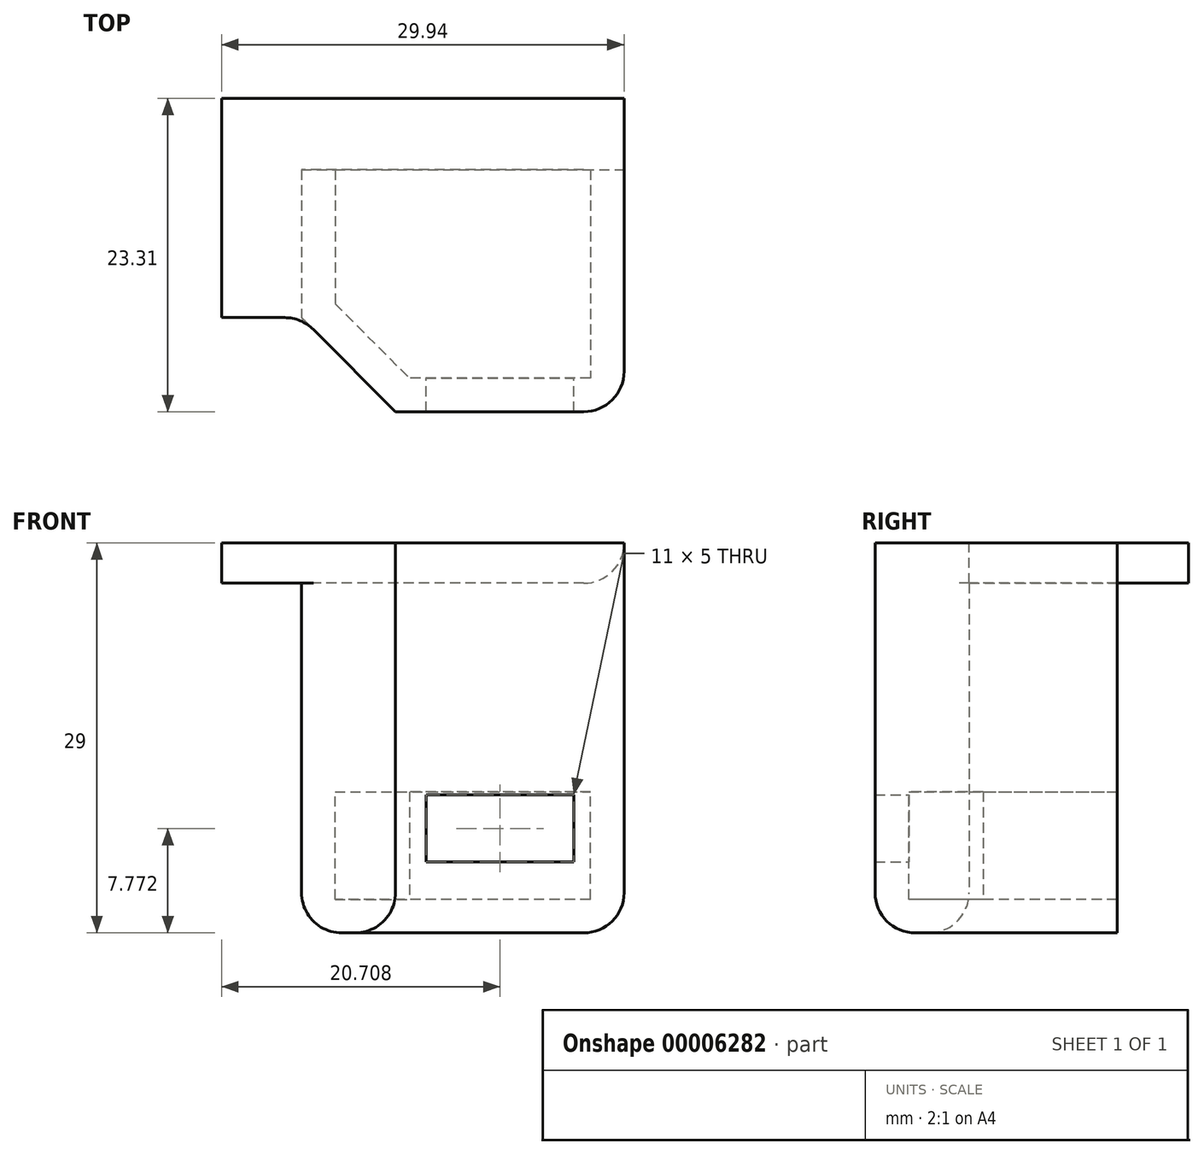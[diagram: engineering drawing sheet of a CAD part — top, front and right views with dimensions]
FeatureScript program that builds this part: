
annotation { "Feature Type Name" : "Feature", "Feature Type Description" : "" }
export const myFeature = defineFeature(function(context is Context, id is Id, definition is map)
    precondition{}
    {
        {
            var Q0;
            Q0=qCreatedBy(makeId("Front.planeOp"),FACE);
            var sketch = newSketch(context, id + "F0", { "sketchPlane" : qUnion([Q0])});
            skLineSegment(sketch, "E0.rect.bottom", {"start": v(12, -14.5) * mm, "end": v(-12, -14.5) * mm});
            skLineSegment(sketch, "E0.rect.top", {"start": v(12, 14.5) * mm, "end": v(-12, 14.5) * mm});
            skLineSegment(sketch, "E0.rect.left", {"start": v(12, -14.5) * mm, "end": v(12, 14.5) * mm});
            skLineSegment(sketch, "E0.rect.right", {"start": v(-12, -14.5) * mm, "end": v(-12, 14.5) * mm});
            skPoint(sketch, "E0.rect.middle", {"position": v(0, 0) * mm});
            skLineSegment(sketch, "E1.rect.bottom", {"start": v(9.3, 4.77) * mm, "end": v(-9.3, 4.77) * mm});
            skLineSegment(sketch, "E1.rect.top", {"start": v(9.3, 12.77) * mm, "end": v(-9.3, 12.77) * mm});
            skLineSegment(sketch, "E1.rect.left", {"start": v(9.3, 4.77) * mm, "end": v(9.3, 12.77) * mm});
            skLineSegment(sketch, "E1.rect.right", {"start": v(-9.3, 4.77) * mm, "end": v(-9.3, 12.77) * mm});
            skPoint(sketch, "E1.rect.middle", {"position": v(0, 8.77) * mm});
            skSolve(sketch);
        }
        {
            var Q0;
            Q0=makeQuery(id+"F0.imprint","IMPRINT",FACE,{"disambiguationData":[TD([[makeQuery(id+"F0.imprint","IMPRINT",EDGE,{"derivedFrom":sQuery(id+"F0.wireOp",EDGE,"E0.rect.bottom")}),-1.0]])]});
            var Q1;
            Q1=makeQuery(id+"F0.imprint","IMPRINT",FACE,{"disambiguationData":[TD([[makeQuery(id+"F0.imprint","IMPRINT",EDGE,{"derivedFrom":sQuery(id+"F0.wireOp",EDGE,"E1.rect.bottom")}),-1.0]])]});
            extrude(context, id + "F1", {"entities" : qUnion([Q0, Q1]), "depth" : 18 * mm});
        }
        {
            var Q0;
            Q0=makeQuery(id+"F1.opExtrude","SWEPT_FACE",FACE,{"disambiguationData":[OSD([sQuery(id+"F0.wireOp",EDGE,"E0.rect.bottom")])]});
            var sketch = newSketch(context, id + "F2", { "sketchPlane" : qUnion([Q0])});
            skLineSegment(sketch, "E2", {"start": v(-12, 7) * mm, "end": v(-5, 0) * mm});
            skLineSegment(sketch, "E3", {"start": v(-5, 0) * mm, "end": v(-12, 0) * mm});
            skLineSegment(sketch, "E4", {"start": v(-12, 0) * mm, "end": v(-12, 7) * mm});
            skSolve(sketch);
        }
        {
            var Q0;
            Q0=makeQuery(id+"F2.imprint","IMPRINT",FACE,{"disambiguationData":[TD([[makeQuery(id+"F2.imprint","IMPRINT",EDGE,{"derivedFrom":sQuery(id+"F2.wireOp",EDGE,"E2")}),-1.0]])]});
            extrude(context, id + "F3", {"entities" : qUnion([Q0]), "operationType" : NewBodyOperationType.REMOVE, "endBound" : BoundingType.THROUGH_ALL, "oppositeDirection" : true, "depth" : 25 * mm});
        }
        {
            var Q0;
            Q0=makeQuery(id+"F1.opExtrude","CAP_FACE",FACE,{"disambiguationData":[OSD([sQuery(id+"F0.wireOp",EDGE,"E0.rect.bottom"),sQuery(id+"F0.wireOp",EDGE,"E0.rect.top"),sQuery(id+"F0.wireOp",EDGE,"E0.rect.left"),sQuery(id+"F0.wireOp",EDGE,"E0.rect.right")])],"isStart":false});
            shell(context, id + "F4", {"entities" : qUnion([Q0]), "thickness" : 2.5 * mm});
        }
        {
            var Q0;
            Q0=makeQuery(id+"F1.opExtrude","CAP_FACE",FACE,{"disambiguationData":[OSD([sQuery(id+"F0.wireOp",EDGE,"E0.rect.bottom"),sQuery(id+"F0.wireOp",EDGE,"E0.rect.top"),sQuery(id+"F0.wireOp",EDGE,"E0.rect.left"),sQuery(id+"F0.wireOp",EDGE,"E0.rect.right")])],"isStart":false});
            var sketch = newSketch(context, id + "F5", { "sketchPlane" : qUnion([Q0])});
            skLineSegment(sketch, "E5.top", {"start": v(-9.5, -4) * mm, "end": v(9.5, -4) * mm});
            skLineSegment(sketch, "E6.0", {"start": v(12, -14.5) * mm, "end": v(12, 14.5) * mm});
            skLineSegment(sketch, "E7", {"start": v(-9.5, -4) * mm, "end": v(-9.5, 12) * mm});
            skLineSegment(sketch, "E8", {"start": v(-9.5, 12) * mm, "end": v(9.5, 12) * mm});
            skLineSegment(sketch, "E9", {"start": v(9.5, 12) * mm, "end": v(9.5, -4) * mm});
            skSolve(sketch);
        }
        {
            var Q0;
            Q0=makeQuery(id+"F5.imprint","IMPRINT",FACE,{"disambiguationData":[TD([[makeQuery(id+"F5.imprint","IMPRINT",EDGE,{"derivedFrom":sQuery(id+"F5.wireOp",EDGE,"E5.top")}),1.0]])]});
            var Q1;
            Q1=makeQuery(id+"F1.opExtrude","SWEPT_BODY",BODY,{"disambiguationData":[OSD([sQuery(id+"F0.wireOp",EDGE,"E0.rect.bottom"),sQuery(id+"F0.wireOp",EDGE,"E0.rect.top"),sQuery(id+"F0.wireOp",EDGE,"E0.rect.left"),sQuery(id+"F0.wireOp",EDGE,"E0.rect.right")])]});
            extrude(context, id + "F6", {"entities" : qUnion([Q0]), "operationType" : NewBodyOperationType.ADD, "endBound" : BoundingType.UP_TO_BODY, "oppositeDirection" : true, "endBoundEntityBody" : qUnion([Q1]), "depth" : 25 * mm});
        }
        {
            var Q0;
            Q0=makeQuery(id+"F1.opExtrude","SWEPT_FACE",FACE,{"disambiguationData":[OSD([sQuery(id+"F0.wireOp",EDGE,"E0.rect.top")])]});
            var sketch = newSketch(context, id + "F7", { "sketchPlane" : qUnion([Q0])});
            skLineSegment(sketch, "E10.left", {"start": v(12, -18) * mm, "end": v(12, 0) * mm});
            skLineSegment(sketch, "E11.bottom", {"start": v(12, -18) * mm, "end": v(-12, -18) * mm});
            skLineSegment(sketch, "E11.top", {"start": v(12, -23.31) * mm, "end": v(-12, -23.31) * mm});
            skLineSegment(sketch, "E11.right", {"start": v(-12, -18) * mm, "end": v(-12, -23.31) * mm});
            skLineSegment(sketch, "E12.bottom", {"start": v(-12, -7) * mm, "end": v(-17.94, -7) * mm});
            skLineSegment(sketch, "E12.top", {"start": v(-12, -23.31) * mm, "end": v(-17.94, -23.31) * mm});
            skLineSegment(sketch, "E12.left", {"start": v(-12, -7) * mm, "end": v(-12, -23.31) * mm});
            skLineSegment(sketch, "E12.right", {"start": v(-17.94, -7) * mm, "end": v(-17.94, -23.31) * mm});
            skLineSegment(sketch, "E13", {"start": v(12, -18) * mm, "end": v(12, -23.31) * mm});
            skPoint(sketch, "E14.orphan", {"position": v(19.4, -23.31) * mm});
            skSolve(sketch);
        }
        {
            var Q0;
            Q0=makeQuery(id+"F7.imprint","IMPRINT",FACE,{"disambiguationData":[TD([[makeQuery(id+"F7.imprint","IMPRINT",EDGE,{"derivedFrom":sQuery(id+"F7.wireOp",EDGE,"E10.top")}),-1.0]])]});
            var Q1;
            {var subQ2=sQuery(id+"F7.wireOp",EDGE,"E11.bottom");Q1=makeQuery(id+"F7.imprint","IMPRINT",FACE,{"disambiguationData":[TD([[makeQuery(id+"F7.imprint","IMPRINT",EDGE,{"derivedFrom":subQ2}),1.0]])]});}
            var Q2;
            {var subQ3=sQuery(id+"F7.wireOp",EDGE,"E12.bottom");Q2=makeQuery(id+"F7.imprint","IMPRINT",FACE,{"disambiguationData":[TD([[makeQuery(id+"F7.imprint","IMPRINT",EDGE,{"derivedFrom":subQ3}),1.0]])]});}
            var Q3;
            Q3=makeQuery(id+"F7.imprint","IMPRINT",FACE,{"disambiguationData":[TD([[makeQuery(id+"F7.imprint","IMPRINT",EDGE,{"derivedFrom":sQuery(id+"F7.wireOp",EDGE,"E10.left")}),1.0]])]});
            extrude(context, id + "F8", {"entities" : qUnion([Q0, Q1, Q2, Q3]), "operationType" : NewBodyOperationType.ADD, "oppositeDirection" : true, "depth" : 3 * mm});
        }
        {
            var Q0;
            Q0=makeQuery(id+"F8.opExtrude","CAP_EDGE",EDGE,{"disambiguationData":[OSD([sQuery(id+"F7.wireOp",EDGE,"E10.left"),sQuery(id+"F7.wireOp",EDGE,"E13")])],"isStart":false});
            var Q1;
            Q1=makeQuery(id+"F8.opExtrude","CAP_EDGE",EDGE,{"disambiguationData":[OSD([sQuery(id+"F7.wireOp",EDGE,"E11.bottom")])],"isStart":false});
            fillet(context, id + "F9", {"entities" : qUnion([Q0, Q1]), "radius" : 3 * mm, "tangentPropagation" : true, "allowEdgeOverflow" : false});
        }
        {
            var Q0;
            Q0=makeQuery(id+"F1.opExtrude","CAP_EDGE",EDGE,{"disambiguationData":[OSD([sQuery(id+"F0.wireOp",EDGE,"E0.rect.bottom")])],"isStart":true});
            var Q1;
            Q1=makeQuery(id+"F1.opExtrude","SWEPT_EDGE",EDGE,{"disambiguationData":[OSD([sQuery(id+"F0.wireOp",EDGE,"E0.rect.bottom"),sQuery(id+"F0.wireOp",EDGE,"E0.rect.left")])]});
            var Q2;
            Q2=makeQuery(id+"F3.boolean.opBoolean","COPY",EDGE,{"derivedFrom":makeQuery(id+"F3.opExtrude","CAP_EDGE",EDGE,{"disambiguationData":[OSD([sQuery(id+"F2.wireOp",EDGE,"E2")])],"isStart":true})});
            var Q3;
            Q3=makeQuery(id+"F1.opExtrude","SWEPT_EDGE",EDGE,{"disambiguationData":[OSD([sQuery(id+"F0.wireOp",EDGE,"E0.rect.bottom"),sQuery(id+"F0.wireOp",EDGE,"E0.rect.right")])]});
            var Q4;
            Q4=makeQuery(id+"F1.opExtrude","CAP_EDGE",EDGE,{"disambiguationData":[OSD([sQuery(id+"F0.wireOp",EDGE,"E0.rect.left")])],"isStart":true});
            var Q5;
            Q5=makeQuery(id+"F3.boolean.opBoolean","COPY",EDGE,{"derivedFrom":makeQuery(id+"F3.opExtrude","SWEPT_EDGE",EDGE,{"disambiguationData":[OSD([sQuery(id+"F0.wireOp",EDGE,"E0.rect.bottom"),sQuery(id+"F2.wireOp",EDGE,"E2"),sQuery(id+"F2.wireOp",EDGE,"E3")])]})});
            var Q6;
            {var subQ0=sQuery(id+"F2.wireOp",EDGE,"E2");Q6=makeQuery(id+"F8.boolean.opBoolean","MERGE",EDGE,{"derivedFrom":[makeQuery(id+"F3.boolean.opBoolean","COPY",EDGE,{"derivedFrom":makeQuery(id+"F3.opExtrude","SWEPT_EDGE",EDGE,{"disambiguationData":[OSD([sQuery(id+"F0.wireOp",EDGE,"E0.rect.bottom"),sQuery(id+"F0.wireOp",EDGE,"E0.rect.right"),subQ0,sQuery(id+"F2.wireOp",EDGE,"E4")])]})}),makeQuery(id+"F8.opExtrude","SWEPT_EDGE",EDGE,{"disambiguationData":[OSD([sQuery(id+"F0.wireOp",EDGE,"E0.rect.top"),subQ0,sQuery(id+"F7.wireOp",EDGE,"E12.bottom"),sQuery(id+"F7.wireOp",EDGE,"E12.left")])]})]});}
            fillet(context, id + "F10", {"entities" : qUnion([Q0, Q1, Q2, Q3, Q4, Q5, Q6]), "radius" : 3 * mm, "tangentPropagation" : true, "allowEdgeOverflow" : false});
        }
        {
            var Q0;
            Q0=makeQuery(id+"F4.opShell","OFFSET_FACE",FACE,{"disambiguationData":[OSD([sQuery(id+"F0.wireOp",EDGE,"E0.rect.bottom"),sQuery(id+"F0.wireOp",EDGE,"E0.rect.top"),sQuery(id+"F0.wireOp",EDGE,"E0.rect.left"),sQuery(id+"F0.wireOp",EDGE,"E0.rect.right")])]});
            var sketch = newSketch(context, id + "F11", { "sketchPlane" : qUnion([Q0])});
            skLineSegment(sketch, "E15.0", {"start": v(9.5, -12) * mm, "end": v(-9.5, -12) * mm});
            skLineSegment(sketch, "E16.0", {"start": v(9.5, -12) * mm, "end": v(9.5, -4) * mm});
            skLineSegment(sketch, "E17.0", {"start": v(-9.5, -4) * mm, "end": v(9.5, -4) * mm});
            skLineSegment(sketch, "E18.0", {"start": v(-3.96, -4) * mm, "end": v(-3.96, -12) * mm});
            skLineSegment(sketch, "E19", {"start": v(2.77, -12) * mm, "end": v(2.77, -4) * mm, "construction": true});
            skLineSegment(sketch, "E20", {"start": v(2.77, -4) * mm, "end": v(9.5, -8) * mm, "construction": true});
            skLineSegment(sketch, "E21", {"start": v(9.5, -8) * mm, "end": v(-3.96, -8) * mm, "construction": true});
            skLineSegment(sketch, "E22.rect.bottom", {"start": v(-2.73, -4.23) * mm, "end": v(8.27, -4.23) * mm});
            skLineSegment(sketch, "E22.rect.top", {"start": v(-2.73, -9.23) * mm, "end": v(8.27, -9.23) * mm});
            skLineSegment(sketch, "E22.rect.left", {"start": v(-2.73, -4.23) * mm, "end": v(-2.73, -9.23) * mm});
            skLineSegment(sketch, "E22.rect.right", {"start": v(8.27, -4.23) * mm, "end": v(8.27, -9.23) * mm});
            skPoint(sketch, "E22.rect.middle", {"position": v(2.77, -6.73) * mm});
            skSolve(sketch);
        }
        {
            var Q0;
            Q0=makeQuery(id+"F11.imprint","IMPRINT",FACE,{"disambiguationData":[TD([[makeQuery(id+"F11.imprint","IMPRINT",EDGE,{"derivedFrom":sQuery(id+"F11.wireOp",EDGE,"E22.rect.bottom")}),-1.0]])]});
            extrude(context, id + "F12", {"entities" : qUnion([Q0]), "operationType" : NewBodyOperationType.REMOVE, "oppositeDirection" : true, "depth" : 25 * mm});
        }
        {
            var Q0;
            Q0=makeQuery(id+"F1.opExtrude","SWEPT_BODY",BODY,{"disambiguationData":[OSD([sQuery(id+"F0.wireOp",EDGE,"E0.rect.bottom"),sQuery(id+"F0.wireOp",EDGE,"E0.rect.top"),sQuery(id+"F0.wireOp",EDGE,"E0.rect.left"),sQuery(id+"F0.wireOp",EDGE,"E0.rect.right")])]});
            var Q1;
            Q1=qCreatedBy(makeId("Front.planeOp"),FACE);
            mirror(context, id + "F13", {"entities" : qUnion([Q0]), "mirrorPlane" : qUnion([Q1])});
        }
        {
            var Q0;
            Q0=makeQuery(id+"F13.opPattern","COPY",BODY,{"derivedFrom":makeQuery(id+"F1.opExtrude","SWEPT_BODY",BODY,{"disambiguationData":[OSD([sQuery(id+"F0.wireOp",EDGE,"E0.rect.bottom"),sQuery(id+"F0.wireOp",EDGE,"E0.rect.top"),sQuery(id+"F0.wireOp",EDGE,"E0.rect.left"),sQuery(id+"F0.wireOp",EDGE,"E0.rect.right")])]}),"instanceName":"1"});
            var Q1;
            Q1=qCreatedBy(makeId("Front.planeOp"),FACE);
            transform(context, id + "F14", {"entities" : qUnion([Q0]), "transformType" : TransformType.TRANSLATION_DISTANCE, "transformDirection" : qUnion([Q1]), "distance" : 5 * mm, "oppositeDirection" : true, "makeCopy" : false});
        }
        {
            var Q0;
            Q0=makeQuery(id+"F1.opExtrude","SWEPT_BODY",BODY,{"disambiguationData":[OSD([sQuery(id+"F0.wireOp",EDGE,"E0.rect.bottom"),sQuery(id+"F0.wireOp",EDGE,"E0.rect.top"),sQuery(id+"F0.wireOp",EDGE,"E0.rect.left"),sQuery(id+"F0.wireOp",EDGE,"E0.rect.right")])]});
            deleteBodies(context, id + "F15", {"entities" : qUnion([Q0])});
        }
    });
